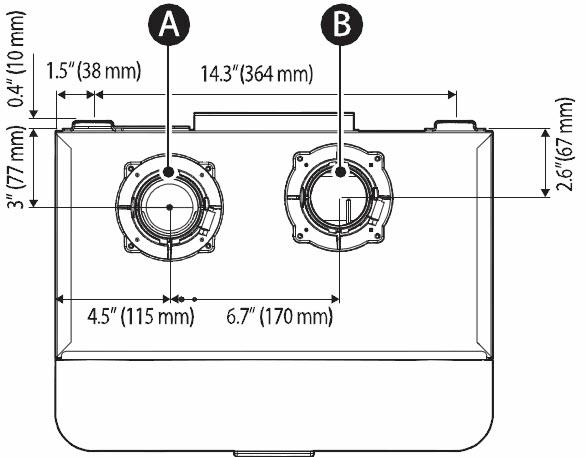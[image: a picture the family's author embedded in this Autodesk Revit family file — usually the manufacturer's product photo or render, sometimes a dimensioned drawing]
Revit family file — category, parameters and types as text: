
# Revit family: Water_Heater-Racks-Navien-NPE-15_Unit_Front---
name_source: partatom
category: Mechanical Equipment
revit_build: Autodesk Revit 2016 (Build: 20150220_1215(x64)
units: mm (PartAtom-declared; Revit-internal decimal feet)

## family parameters
Cut with Voids When Loaded = No
Host = Face
OmniClass Number = 23.65.35.11
OmniClass Title = Supply Water Heaters
Part Type = Normal
Room Calculation Point = No
Round Connector Dimension = Use Diameter
Shared = No

## types (4) — shared parameters
2" Exhaust/Intake = Yes
3" Exhaust/Intake = No
Apparent Load = 0 VA
Assembly Code = D3010500
Certifications = Energy Star | AHRI | CSA | CSA | NFS
Cold Water Inlet = 1"
Configuration = NPE_F15_4F4F-4F3F
Default Elevation = 48 "
Depth = 23.8 "
Description = 15 Unit Front
Exhaust = 2"
Finish = Metal - Navien - White
Flow Rate = 1 GPM
Flow Rate Note = 35°F (19°C) temp rise: 11.2 GPM (42 L/m) | 45°F (25°C) temp rise: 8.7 GPM (33 L/m) | 67°F (36°C) temp rise: NPE-240A: 5.6 GPM(21 L/m), NPE-240S: 5.7 GPM(22 L/m)
Frequency = 60 Hz
Gas Inlet = 1"
Heating Capacity = 120000.0 Btu/h
Heating Capacity Note = 19,900–199,900 (BTU/H)
Height = 65.5 "
Hot Water Outlet = 1"
Ignition = Electronic ignition
Installation Type = Indoor
Intake = 2"
Keynote = 22 33 00.A1
Manifold(s) = (1) 30019041A + (3) 30019043A
Manufacturer = Navien, Inc.
Manufacturer Fax Number = (949) 420-0430
Natural Gas Manifold Pressure = -0.05" WC to -0.58" WC
Natural Gas Supply Pressure = 3.5"–10.5" WC
Number of Poles = 1
Phase = 1
Power Factor = 1
Product Documentation Link = https://www.navieninc.com
Product Name = NPE Series Tankless Water Heaters w/ Racks
Product Page URL = https://www.navieninc.com
Propane Gas Manifold Pressure = -0.10" WC to -0.78" WC
Propane Gas Supply Pressure = 8"–13" WC
Rack(s) = (2) GFFM-KDIZUS-003 + (13) GFFM-KDIZUS-004
Required Cascade Operation Accessory = (15) 30014367A (Common Vent Damper & Cascade Communication Cable) or (14) GXXX000546 (Individual Vent Cascade Communication Cable)
Type Comments = For Wall Mount RL Manifold systems- Exclude Base & Add-on Racks
URL = https://www.navieninc.com
Venting = Exhaust: 2" PVC, CPVC, PP, SS / 2" special gas vent type BH (Class II, A/B/C) | Intake: 2" PVC, CPVC, PP, SS / 2" special gas vent type BH (Class II, A/B/C) | Vent clearances: 0" to combustibles
Venting Type = Forced draft direct vent
Version = 2016 - v1.0.a
Voltage = 120 V
Water Pressure = 15–150 PSI
Wi-Fi Ready = NaviLink Wi-Fi Control: PBCM-AS-001
Width = 322.3 "

## per-type parameters (varying)
| type | Constraints | Model | Natural Gas | Propane Gas | Recirculation Inlet | Recirculation Inlet Visibility | Tankless Water Heaters | Weight |
| Natural Gas - Recirculating System - NPE-240A(Advanced)-NG | 6 | (15) NPE-240A-NG | Yes | No | 0" | Yes | (15) NPE-240A-NG | 82.00 lbf |
| Natural Gas - NPE-240S(Standard)-NG | 7 | (15) NPE-240S-NG | Yes | No | 1" | No | (15) NPE-240S-NG | 75.00 lbf |
| Propane Gas - Recirculating System - NPE-240A(Advanced)-LPG | 6 | (15) NPE-240A-LPG | No | Yes | 0" | Yes | (15) NPE-240A-LPG | 82.00 lbf |
| Propane Gas - NPE-240S(Standard)-LPG | 7 | (15) NPE-240S-LPG | No | Yes | 1" | No | (15) NPE-240S-LPG | 75.00 lbf |

## geometry (parser evidence)
native form markers: Sweep x19
no freeform markers — native parametric forms only
